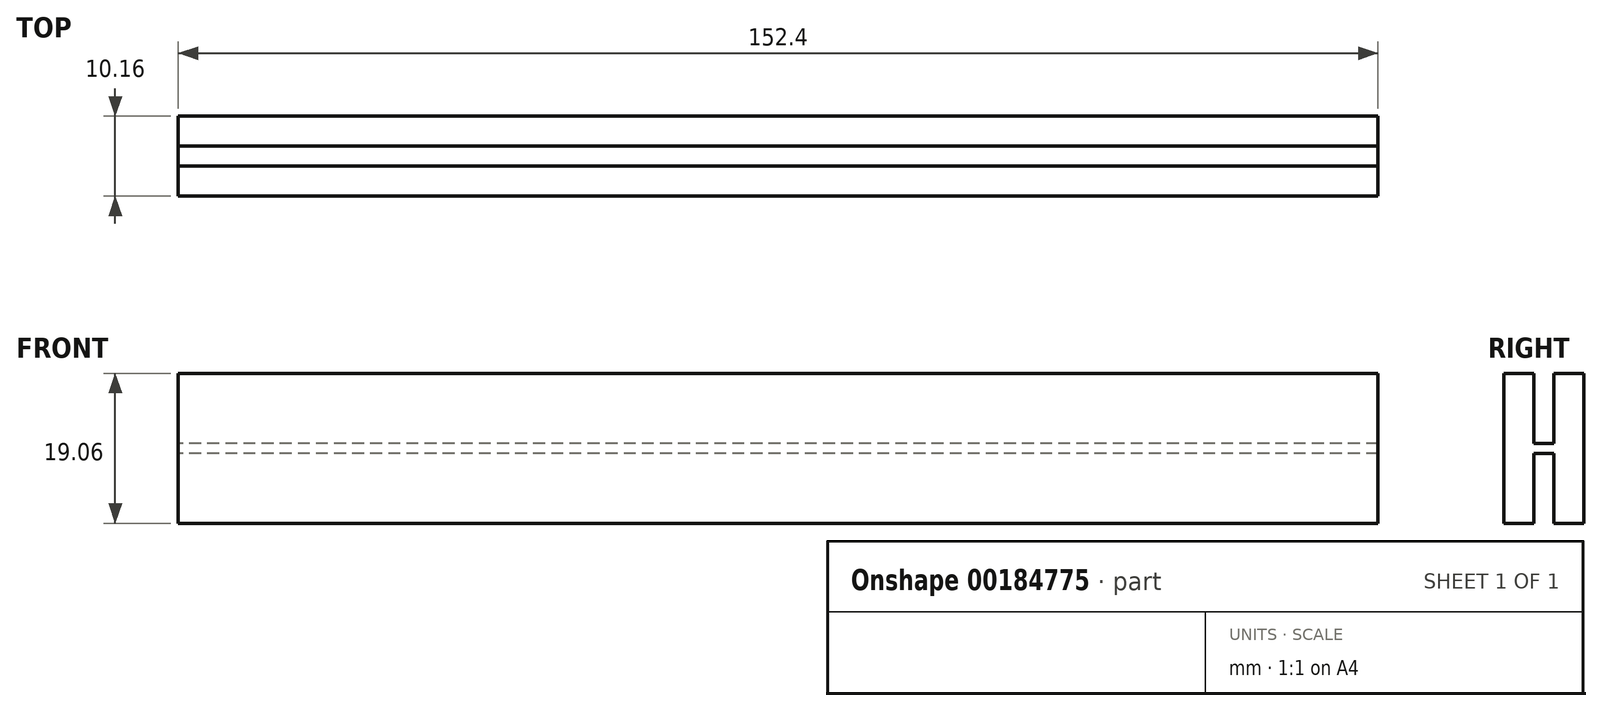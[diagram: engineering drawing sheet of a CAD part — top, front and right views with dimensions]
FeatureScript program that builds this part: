
annotation { "Feature Type Name" : "Feature", "Feature Type Description" : "" }
export const myFeature = defineFeature(function(context is Context, id is Id, definition is map)
    precondition{}
    {
        {
            var Q0;
            Q0=qCreatedBy(makeId("Front.planeOp"),FACE);
            var sketch = newSketch(context, id + "F0", { "sketchPlane" : qUnion([Q0])});
            skLineSegment(sketch, "E0.bottom", {"start": v(76.2, 9.53) * mm, "end": v(-76.2, 9.53) * mm});
            skLineSegment(sketch, "E0.top", {"start": v(76.2, -9.53) * mm, "end": v(-76.2, -9.53) * mm});
            skLineSegment(sketch, "E0.left", {"start": v(76.2, 9.53) * mm, "end": v(76.2, -9.53) * mm});
            skLineSegment(sketch, "E0.right", {"start": v(-76.2, 9.53) * mm, "end": v(-76.2, -9.53) * mm});
            skPoint(sketch, "E0.middle", {"position": v(0, 0) * mm});
            skSolve(sketch);
        }
        {
            var Q0;
            Q0=makeQuery(id+"F0.imprint","IMPRINT",FACE,{"disambiguationData":[TD([[makeQuery(id+"F0.imprint","IMPRINT",EDGE,{"derivedFrom":sQuery(id+"F0.wireOp",EDGE,"E0.bottom")}),1.0]])]});
            extrude(context, id + "F1", {"entities" : qUnion([Q0]), "endBound" : BoundingType.SYMMETRIC, "depth" : 10.16 * mm});
        }
        {
            var Q0;
            Q0=makeQuery(id+"F1.opExtrude","SWEPT_FACE",FACE,{"disambiguationData":[OSD([sQuery(id+"F0.wireOp",EDGE,"E0.right")])]});
            var sketch = newSketch(context, id + "F2", { "sketchPlane" : qUnion([Q0])});
            skLineSegment(sketch, "E1.bottom", {"start": v(-1.27, 9.52) * mm, "end": v(1.27, 9.52) * mm});
            skLineSegment(sketch, "E1.top", {"start": v(-1.27, -9.52) * mm, "end": v(1.27, -9.52) * mm});
            skLineSegment(sketch, "E1.left", {"start": v(-1.27, 9.52) * mm, "end": v(-1.27, -9.52) * mm});
            skLineSegment(sketch, "E1.right", {"start": v(1.27, 9.52) * mm, "end": v(1.27, -9.52) * mm});
            skPoint(sketch, "E1.middle", {"position": v(0, 0) * mm});
            skLineSegment(sketch, "E2.bottom", {"start": v(-1.27, -0.64) * mm, "end": v(1.27, -0.64) * mm});
            skLineSegment(sketch, "E2.top", {"start": v(-1.27, 0.64) * mm, "end": v(1.27, 0.64) * mm});
            skPoint(sketch, "E2.right.end.orphan", {"position": v(5.08, 0.64) * mm});
            skPoint(sketch, "E2.right.start.orphan", {"position": v(5.08, -0.64) * mm});
            skPoint(sketch, "E2.left.end.orphan", {"position": v(-5.08, 0.64) * mm});
            skPoint(sketch, "E2.left.start.orphan", {"position": v(-5.08, -0.64) * mm});
            skSolve(sketch);
        }
        {
            var Q0;
            {var subQ0=sQuery(id+"F2.wireOp",EDGE,"E1.bottom");Q0=makeQuery(id+"F2.imprint","IMPRINT",FACE,{"disambiguationData":[TD([[makeQuery(id+"F2.imprint","IMPRINT",EDGE,{"derivedFrom":subQ0}),1.0]])]});}
            var Q1;
            {var subQ0=sQuery(id+"F2.wireOp",EDGE,"E1.top");Q1=makeQuery(id+"F2.imprint","IMPRINT",FACE,{"disambiguationData":[TD([[makeQuery(id+"F2.imprint","IMPRINT",EDGE,{"derivedFrom":subQ0}),-1.0]])]});}
            extrude(context, id + "F3", {"entities" : qUnion([Q0, Q1]), "operationType" : NewBodyOperationType.REMOVE, "oppositeDirection" : true, "depth" : 152.4 * mm});
        }
    });
